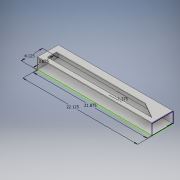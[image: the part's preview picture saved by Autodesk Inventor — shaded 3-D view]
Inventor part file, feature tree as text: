
AUTODESK INVENTOR PART (.ipt)
format: ipt  version: 2019 (Build 230136000, 136)  size: 189,440 bytes
history: native  units: in
note: dims shown in document units (in); Inventor stores cm internally (conversion verified against a paired STEP export)
features: extrude x8, sketch x7
ambient origin geometry x8: Origin, YZ Plane, XZ Plane, XY Plane, X Axis, Y Axis, Z Axis, Center Point
bodies: Solid1 (feature_tree)
feature tree (15):
  sketch  "Sketch1"  dims[d0=4.125in d1=22.125in]
  extrude  "Extrusion1"  Depth=22.125in
  extrude  "Extrusion2"  Depth=21.875in
  extrude  "Extrusion3"  Depth=0.125in TaperAngle=0.0deg
  extrude  "Extrusion4"  Depth=22.125in
  extrude  "Extrusion5"  Depth=22.125in
  extrude  "Extrusion6"  Depth=1.0in
  extrude  "Extrusion7"  Depth=1.0in
  extrude  "Extrusion9"  Depth=0.125in TaperAngle=0.0deg
  sketch  "Sketch2"  dims[d2=1.375in d3=21.875in]
  sketch  "Sketch3"  dims[d4=3.875in d5=0.125in d6=0.0in]
  sketch  "Sketch4"  dims[d7=2.0in d8=0.0in d9=22.125in]
  sketch  "Sketch5"  dims[d10=1.0in d11=22.125in]
  sketch  "Sketch6"  dims[d12=1.375in d13=1.0in]
  sketch  "Sketch8"  dims[d14=4.125in d15=1.0in d16=0.125in d17=0.0in d18=0.125in d19=21.875in d20=21.875in d21=0.125in d22=0.125in d23=0.0in d24=0.125in d25=0.0in d26=150.0deg d27=0.125in d28=0.0in d29=0.125in d30=0.0in d36=0.065in d37=1.005in d38=0.125in d39=0.0in]
